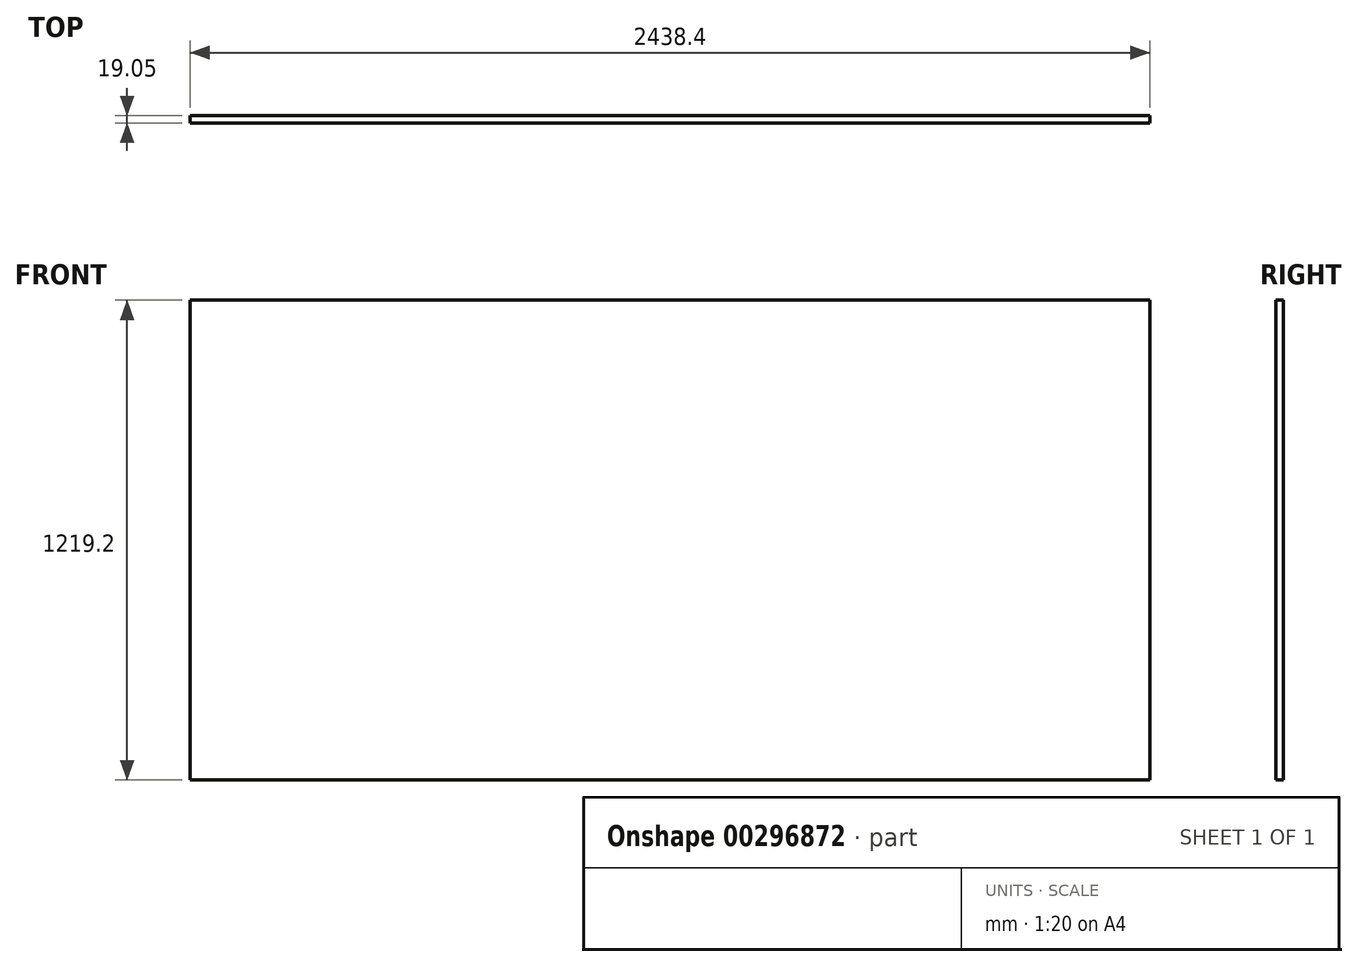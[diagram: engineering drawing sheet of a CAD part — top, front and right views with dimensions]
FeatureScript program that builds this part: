
annotation { "Feature Type Name" : "Feature", "Feature Type Description" : "" }
export const myFeature = defineFeature(function(context is Context, id is Id, definition is map)
    precondition{}
    {
        {
            var Q0;
            Q0=qCreatedBy(makeId("Front.planeOp"),FACE);
            var sketch = newSketch(context, id + "F0", { "sketchPlane" : qUnion([Q0])});
            skLineSegment(sketch, "E0.bottom", {"start": v(-1219.2, 1219.2) * mm, "end": v(1219.2, 1219.2) * mm});
            skLineSegment(sketch, "E0.top", {"start": v(-1219.2, 0) * mm, "end": v(1219.2, 0) * mm});
            skLineSegment(sketch, "E0.left", {"start": v(-1219.2, 1219.2) * mm, "end": v(-1219.2, 0) * mm});
            skLineSegment(sketch, "E0.right", {"start": v(1219.2, 1219.2) * mm, "end": v(1219.2, 0) * mm});
            skSolve(sketch);
        }
        {
            var Q0;
            Q0 = qSketchRegion(id + "F0", true);
            extrude(context, id + "F1", {"entities" : qUnion([Q0]), "depth" : 19.05 * mm});
        }
    });
